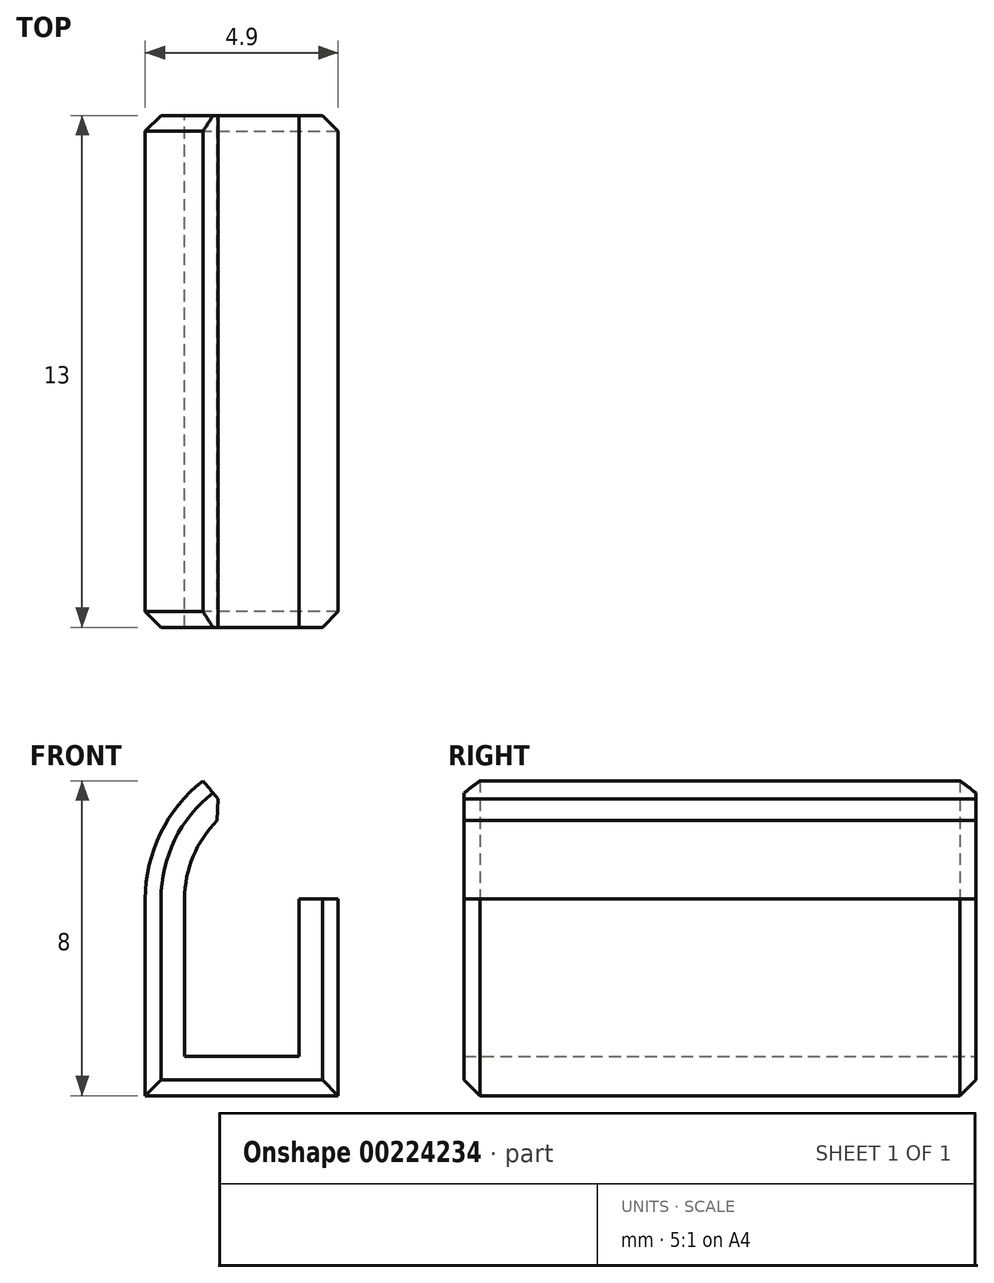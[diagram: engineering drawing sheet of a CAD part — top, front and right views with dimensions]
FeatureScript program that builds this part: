
annotation { "Feature Type Name" : "Feature", "Feature Type Description" : "" }
export const myFeature = defineFeature(function(context is Context, id is Id, definition is map)
    precondition{}
    {
        {
            var Q0;
            Q0=qCreatedBy(makeId("Front.planeOp"),FACE);
            var sketch = newSketch(context, id + "F0", { "sketchPlane" : qUnion([Q0])});
            skLineSegment(sketch, "E0", {"start": v(0, 0) * mm, "end": v(0, 5) * mm});
            skLineSegment(sketch, "E1", {"start": v(0, 5) * mm, "end": v(0, 8) * mm, "construction": true});
            skArc(sketch, "E2", {"start": v(1.46, 8) * mm, "mid": v(0.39, 6.67) * mm, "end": v(0, 5) * mm});
            skLineSegment(sketch, "E3", {"start": v(1.46, 8) * mm, "end": v(2.1, 7.23) * mm});
            skLineSegment(sketch, "E4", {"start": v(0, 0) * mm, "end": v(4.9, 0) * mm});
            skLineSegment(sketch, "E5", {"start": v(4.9, 0) * mm, "end": v(4.9, 5) * mm});
            skLineSegment(sketch, "E6", {"start": v(1, 1) * mm, "end": v(1, 5) * mm});
            skArc(sketch, "E7", {"start": v(2.1, 7.23) * mm, "mid": v(1.3, 6.25) * mm, "end": v(1, 5) * mm});
            skLineSegment(sketch, "E8", {"start": v(4.9, 5) * mm, "end": v(3.9, 5) * mm});
            skLineSegment(sketch, "E9", {"start": v(3.9, 5) * mm, "end": v(3.9, 1) * mm});
            skLineSegment(sketch, "E10", {"start": v(3.9, 1) * mm, "end": v(1, 1) * mm});
            skSolve(sketch);
        }
        {
            var Q0;
            Q0 = qSketchRegion(id + "F0", true);
            extrude(context, id + "F1", {"entities" : qUnion([Q0]), "depth" : 13 * mm});
        }
        {
            var Q0;
            Q0=makeQuery(id+"F1.opExtrude","CAP_EDGE",EDGE,{"disambiguationData":[OSD([sQuery(id+"F0.wireOp",EDGE,"E0")])],"isStart":false});
            var Q1;
            Q1=makeQuery(id+"F1.opExtrude","CAP_EDGE",EDGE,{"disambiguationData":[OSD([sQuery(id+"F0.wireOp",EDGE,"E0")])],"isStart":true});
            var Q2;
            Q2=makeQuery(id+"F1.opExtrude","SWEPT_EDGE",EDGE,{"disambiguationData":[OSD([sQuery(id+"F0.wireOp",EDGE,"E3"),sQuery(id+"F0.wireOp",EDGE,"E7")])]});
            var Q3;
            Q3=makeQuery(id+"F1.opExtrude","CAP_EDGE",EDGE,{"disambiguationData":[OSD([sQuery(id+"F0.wireOp",EDGE,"E4")])],"isStart":true});
            var Q4;
            Q4=makeQuery(id+"F1.opExtrude","CAP_EDGE",EDGE,{"disambiguationData":[OSD([sQuery(id+"F0.wireOp",EDGE,"E5")])],"isStart":true});
            var Q5;
            Q5=makeQuery(id+"F1.opExtrude","CAP_EDGE",EDGE,{"disambiguationData":[OSD([sQuery(id+"F0.wireOp",EDGE,"E5")])],"isStart":false});
            var Q6;
            Q6=makeQuery(id+"F1.opExtrude","CAP_EDGE",EDGE,{"disambiguationData":[OSD([sQuery(id+"F0.wireOp",EDGE,"E4")])],"isStart":false});
            chamfer(context, id + "F2", {"entities" : qUnion([Q0, Q1, Q2, Q3, Q4, Q5, Q6]), "width" : .4 * mm, "tangentPropagation" : true});
        }
    });
